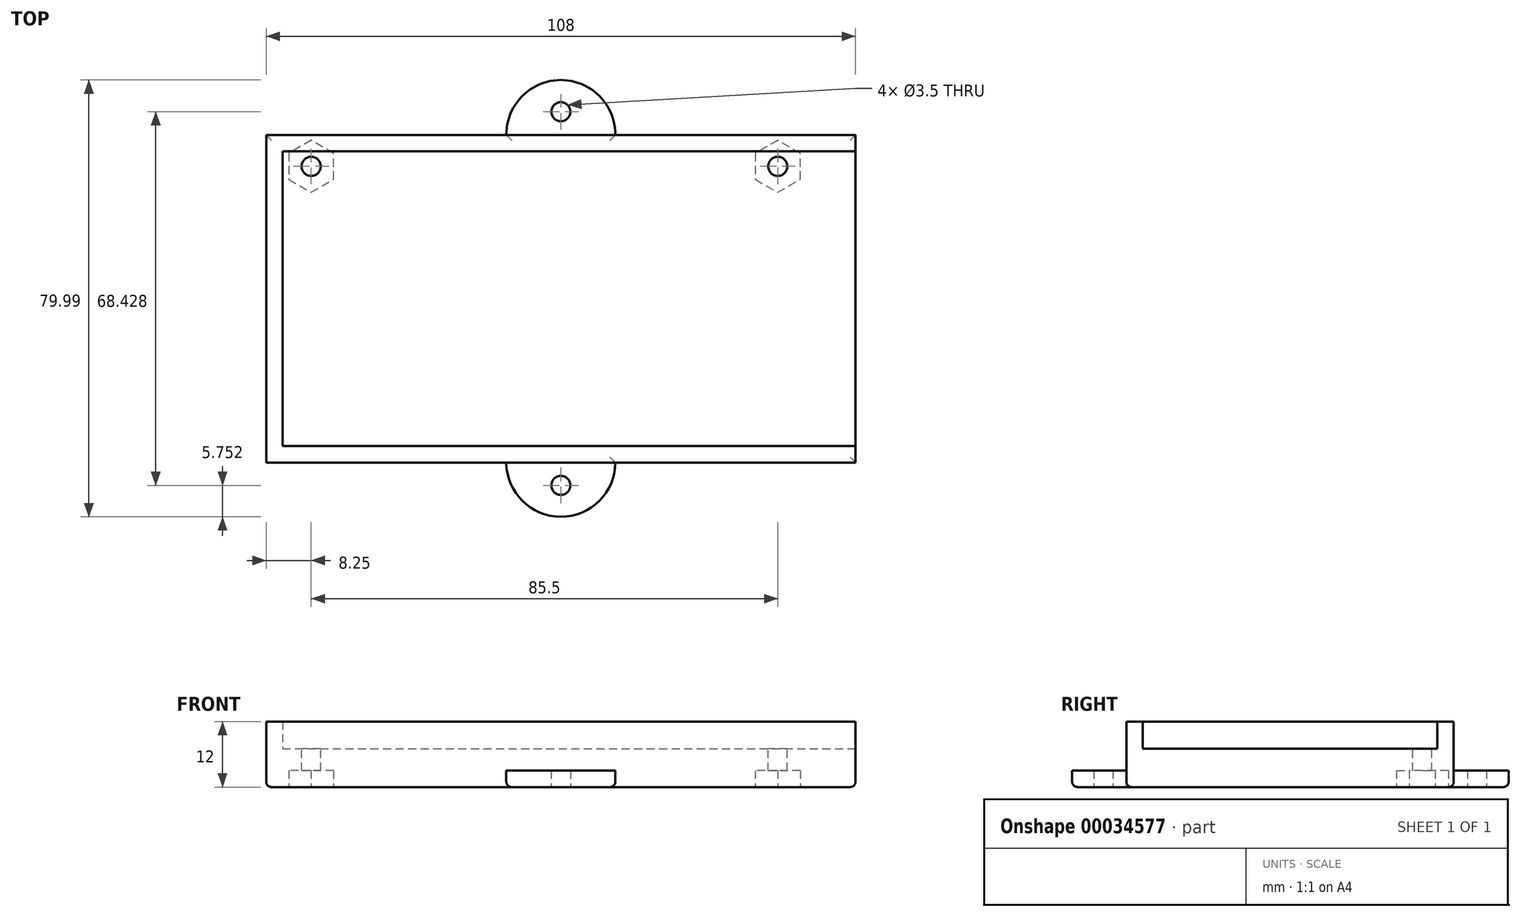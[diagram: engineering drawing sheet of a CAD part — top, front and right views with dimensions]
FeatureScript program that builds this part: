
annotation { "Feature Type Name" : "Feature", "Feature Type Description" : "" }
export const myFeature = defineFeature(function(context is Context, id is Id, definition is map)
    precondition{}
    {
        {
            var Q0;
            Q0=qCreatedBy(makeId("Top.planeOp"),FACE);
            var sketch = newSketch(context, id + "F0", { "sketchPlane" : qUnion([Q0])});
            skLineSegment(sketch, "E0.rect.bottom", {"start": v(-54, 30) * mm, "end": v(54, 30) * mm});
            skLineSegment(sketch, "E0.rect.top", {"start": v(-54, -30) * mm, "end": v(54, -30) * mm});
            skLineSegment(sketch, "E0.rect.left", {"start": v(-54, 30) * mm, "end": v(-54, -30) * mm});
            skLineSegment(sketch, "E0.rect.right", {"start": v(54, 30) * mm, "end": v(54, -30) * mm});
            skPoint(sketch, "E0.rect.middle", {"position": v(0, 0) * mm});
            skSolve(sketch);
        }
        {
            var Q0;
            Q0 = qSketchRegion(id + "F0", true);
            extrude(context, id + "F1", {"entities" : qUnion([Q0]), "depth" : 7 * mm});
        }
        {
            var Q0;
            Q0=makeQuery(id+"F1.opExtrude","CAP_FACE",FACE,{"disambiguationData":[OSD([sQuery(id+"F0.wireOp",EDGE,"E0.rect.bottom"),sQuery(id+"F0.wireOp",EDGE,"E0.rect.top"),sQuery(id+"F0.wireOp",EDGE,"E0.rect.left"),sQuery(id+"F0.wireOp",EDGE,"E0.rect.right")])],"isStart":false});
            var sketch = newSketch(context, id + "F2", { "sketchPlane" : qUnion([Q0])});
            skLineSegment(sketch, "E1.bottom", {"start": v(-54, 30) * mm, "end": v(54, 30) * mm});
            skLineSegment(sketch, "E1.top", {"start": v(-54, -30) * mm, "end": v(54, -30) * mm});
            skLineSegment(sketch, "E1.left", {"start": v(-54, 30) * mm, "end": v(-54, -30) * mm});
            skLineSegment(sketch, "E2.bottom", {"start": v(-51, 27) * mm, "end": v(51, 27) * mm});
            skLineSegment(sketch, "E2.top", {"start": v(-51, -27) * mm, "end": v(51, -27) * mm});
            skLineSegment(sketch, "E2.left", {"start": v(-51, 27) * mm, "end": v(-51, -27) * mm});
            skLineSegment(sketch, "E3", {"start": v(51, 27) * mm, "end": v(54, 27) * mm});
            skLineSegment(sketch, "E4", {"start": v(54, 27) * mm, "end": v(54, 30) * mm});
            skLineSegment(sketch, "E5", {"start": v(51, -27) * mm, "end": v(54, -27) * mm});
            skLineSegment(sketch, "E6", {"start": v(54, -27) * mm, "end": v(54, -30) * mm});
            skSolve(sketch);
        }
        {
            var Q0;
            Q0 = qSketchRegion(id + "F2", true);
            extrude(context, id + "F3", {"entities" : qUnion([Q0]), "operationType" : NewBodyOperationType.ADD, "depth" : 5 * mm});
        }
        {
            var Q0;
            Q0=makeQuery(id+"F1.opExtrude","CAP_FACE",FACE,{"disambiguationData":[OSD([sQuery(id+"F0.wireOp",EDGE,"E0.rect.bottom"),sQuery(id+"F0.wireOp",EDGE,"E0.rect.top"),sQuery(id+"F0.wireOp",EDGE,"E0.rect.left"),sQuery(id+"F0.wireOp",EDGE,"E0.rect.right")])],"isStart":false});
            var sketch = newSketch(context, id + "F4", { "sketchPlane" : qUnion([Q0])});
            skCircle(sketch, "E7", {"center": v(-45.75, 24.25) * mm, "radius": 1.75 * mm});
            skCircle(sketch, "E8", {"center": v(39.75, 24.25) * mm, "radius": 1.75 * mm});
            skSolve(sketch);
        }
        {
            var Q0;
            Q0 = qSketchRegion(id + "F4", true);
            extrude(context, id + "F5", {"entities" : qUnion([Q0]), "operationType" : NewBodyOperationType.REMOVE, "endBound" : BoundingType.THROUGH_ALL, "oppositeDirection" : true, "depth" : 25 * mm});
        }
        {
            var Q0;
            Q0=makeQuery(id+"F1.opExtrude","CAP_FACE",FACE,{"disambiguationData":[OSD([sQuery(id+"F0.wireOp",EDGE,"E0.rect.bottom"),sQuery(id+"F0.wireOp",EDGE,"E0.rect.top"),sQuery(id+"F0.wireOp",EDGE,"E0.rect.left"),sQuery(id+"F0.wireOp",EDGE,"E0.rect.right")])],"isStart":true});
            var sketch = newSketch(context, id + "F6", { "sketchPlane" : qUnion([Q0])});
            skCircle(sketch, "E9.cCircle", {"center": v(39.75, -24.25) * mm, "radius": 4.12 * mm, "construction": true});
            skLineSegment(sketch, "E9.0", {"start": v(35.63, -26.63) * mm, "end": v(35.63, -21.87) * mm});
            skLineSegment(sketch, "E9.1", {"start": v(35.63, -21.87) * mm, "end": v(39.75, -19.49) * mm});
            skLineSegment(sketch, "E9.2", {"start": v(39.75, -19.49) * mm, "end": v(43.88, -21.87) * mm});
            skLineSegment(sketch, "E9.3", {"start": v(43.88, -21.87) * mm, "end": v(43.88, -26.63) * mm});
            skLineSegment(sketch, "E9.4", {"start": v(43.88, -26.63) * mm, "end": v(39.75, -29.01) * mm});
            skLineSegment(sketch, "E9.5", {"start": v(39.75, -29.01) * mm, "end": v(35.63, -26.63) * mm});
            skCircle(sketch, "E10.cCircle", {"center": v(-45.75, -24.25) * mm, "radius": 4.12 * mm, "construction": true});
            skLineSegment(sketch, "E10.0", {"start": v(-49.87, -26.63) * mm, "end": v(-49.87, -21.87) * mm});
            skLineSegment(sketch, "E10.1", {"start": v(-49.87, -21.87) * mm, "end": v(-45.75, -19.49) * mm});
            skLineSegment(sketch, "E10.2", {"start": v(-45.75, -19.49) * mm, "end": v(-41.62, -21.87) * mm});
            skLineSegment(sketch, "E10.3", {"start": v(-41.62, -21.87) * mm, "end": v(-41.62, -26.63) * mm});
            skLineSegment(sketch, "E10.4", {"start": v(-41.62, -26.63) * mm, "end": v(-45.75, -29.01) * mm});
            skLineSegment(sketch, "E10.5", {"start": v(-45.75, -29.01) * mm, "end": v(-49.87, -26.63) * mm});
            skPoint(sketch, "E10.0.midPoint", {"position": v(-49.87, -24.25) * mm});
            skSolve(sketch);
        }
        {
            var Q0;
            Q0 = qSketchRegion(id + "F6", true);
            extrude(context, id + "F7", {"entities" : qUnion([Q0]), "operationType" : NewBodyOperationType.REMOVE, "oppositeDirection" : true, "depth" : 3 * mm});
        }
        {
            var Q0;
            Q0=qCreatedBy(makeId("Top.planeOp"),FACE);
            var sketch = newSketch(context, id + "F8", { "sketchPlane" : qUnion([Q0])});
            skLineSegment(sketch, "E11", {"start": v(10, -30) * mm, "end": v(-10, -30) * mm, "construction": true});
            skArc(sketch, "E12", {"start": v(-10, -30) * mm, "mid": v(0, -39.93) * mm, "end": v(10, -30) * mm});
            skCircle(sketch, "E13", {"center": v(0, -34.18) * mm, "radius": 1.75 * mm});
            skLineSegment(sketch, "E14", {"start": v(10, -30) * mm, "end": v(-10, -30) * mm});
            skLineSegment(sketch, "E15", {"start": v(10, 30) * mm, "end": v(-10, 30) * mm});
            skArc(sketch, "E16", {"start": v(10, 30) * mm, "mid": v(0, 40.06) * mm, "end": v(-10, 30) * mm});
            skCircle(sketch, "E17", {"center": v(0, 34.25) * mm, "radius": 1.75 * mm});
            skSolve(sketch);
        }
        {
            var Q0;
            Q0 = qSketchRegion(id + "F8", true);
            extrude(context, id + "F9", {"entities" : qUnion([Q0]), "operationType" : NewBodyOperationType.ADD, "depth" : 3 * mm});
        }
        {
            var Q0;
            Q0=makeQuery(id+"F1.opExtrude","CAP_EDGE",EDGE,{"disambiguationData":[OSD([sQuery(id+"F0.wireOp",EDGE,"E0.rect.right")])],"isStart":true});
            var Q1;
            {var subQ0=sQuery(id+"F0.wireOp",EDGE,"E0.rect.top");var subQ2=sQuery(id+"F0.wireOp",EDGE,"E0.rect.right");Q1=makeQuery(id+"F9.boolean.opBoolean","SPLIT",EDGE,{"disambiguationData":[TD([makeQuery(id+"F1.opExtrude","SWEPT_FACE",FACE,{"disambiguationData":[OSD([subQ2])]})])],"derivedFrom":makeQuery(id+"F1.opExtrude","CAP_EDGE",EDGE,{"disambiguationData":[OSD([subQ0])],"isStart":true})});}
            var Q2;
            Q2=makeQuery(id+"F9.opExtrude","CAP_EDGE",EDGE,{"disambiguationData":[OSD([sQuery(id+"F8.wireOp",EDGE,"E12")])],"isStart":true});
            var Q3;
            Q3=makeQuery(id+"F1.opExtrude","CAP_EDGE",EDGE,{"disambiguationData":[OSD([sQuery(id+"F0.wireOp",EDGE,"E0.rect.left")])],"isStart":true});
            var Q4;
            {var subQ0=sQuery(id+"F0.wireOp",EDGE,"E0.rect.bottom");var subQ2=sQuery(id+"F0.wireOp",EDGE,"E0.rect.left");Q4=makeQuery(id+"F9.boolean.opBoolean","SPLIT",EDGE,{"disambiguationData":[TD([makeQuery(id+"F1.opExtrude","SWEPT_FACE",FACE,{"disambiguationData":[OSD([subQ2])]})])],"derivedFrom":makeQuery(id+"F1.opExtrude","CAP_EDGE",EDGE,{"disambiguationData":[OSD([subQ0])],"isStart":true})});}
            var Q5;
            Q5=makeQuery(id+"F9.opExtrude","CAP_EDGE",EDGE,{"disambiguationData":[OSD([sQuery(id+"F8.wireOp",EDGE,"E16")])],"isStart":true});
            var Q6;
            {var subQ0=sQuery(id+"F0.wireOp",EDGE,"E0.rect.bottom");var subQ2=sQuery(id+"F0.wireOp",EDGE,"E0.rect.right");Q6=makeQuery(id+"F9.boolean.opBoolean","SPLIT",EDGE,{"disambiguationData":[TD([makeQuery(id+"F1.opExtrude","SWEPT_FACE",FACE,{"disambiguationData":[OSD([subQ2])]})])],"derivedFrom":makeQuery(id+"F1.opExtrude","CAP_EDGE",EDGE,{"disambiguationData":[OSD([subQ0])],"isStart":true})});}
            fillet(context, id + "F10", {"entities" : qUnion([Q0, Q1, Q2, Q3, Q4, Q5, Q6]), "radius" : 1 * mm, "tangentPropagation" : true, "allowEdgeOverflow" : false});
        }
    });
